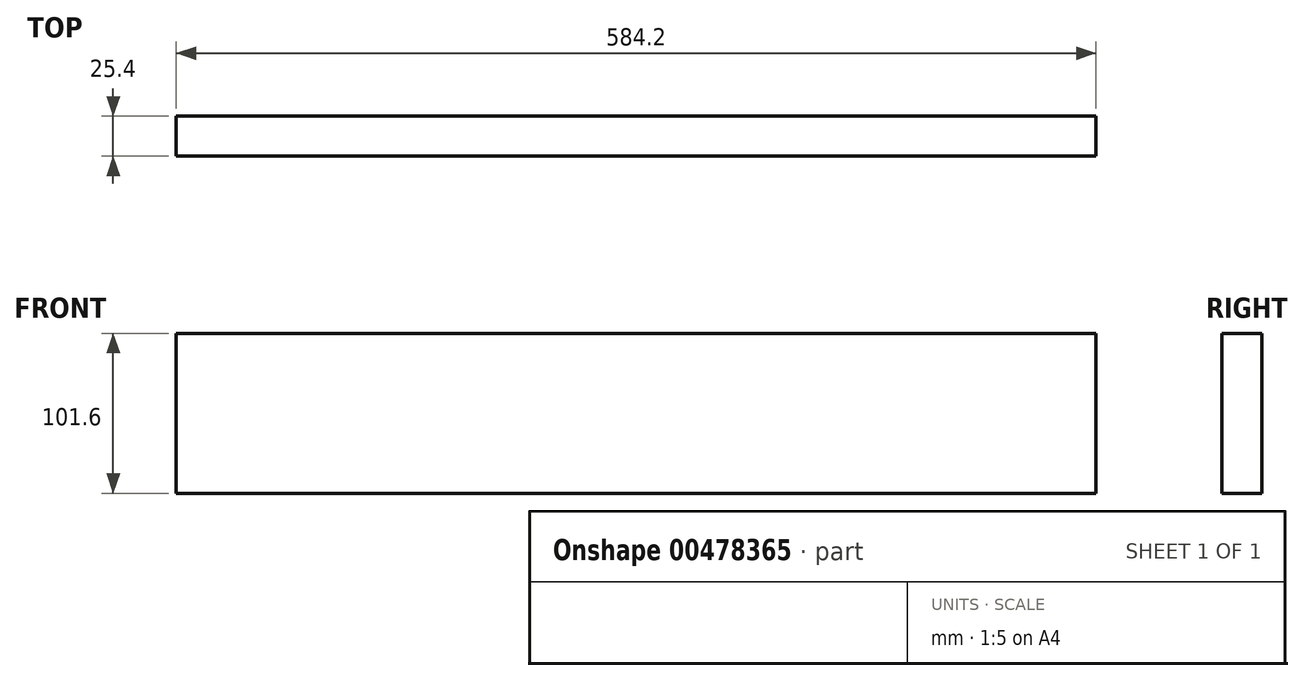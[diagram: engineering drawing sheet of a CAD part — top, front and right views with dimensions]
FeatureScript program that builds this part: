
annotation { "Feature Type Name" : "Feature", "Feature Type Description" : "" }
export const myFeature = defineFeature(function(context is Context, id is Id, definition is map)
    precondition{}
    {
        {
            var Q0;
            Q0=qCreatedBy(makeId("Front.planeOp"),FACE);
            var sketch = newSketch(context, id + "F0", { "sketchPlane" : qUnion([Q0])});
            skLineSegment(sketch, "E0.bottom", {"start": v(-229.27, -46.32) * mm, "end": v(354.93, -46.32) * mm});
            skLineSegment(sketch, "E0.top", {"start": v(-229.27, 55.28) * mm, "end": v(354.93, 55.28) * mm});
            skLineSegment(sketch, "E0.left", {"start": v(-229.27, -46.32) * mm, "end": v(-229.27, 55.28) * mm});
            skLineSegment(sketch, "E0.right", {"start": v(354.93, -46.32) * mm, "end": v(354.93, 55.28) * mm});
            skSolve(sketch);
        }
        {
            var Q0;
            Q0 = qSketchRegion(id + "F0", true);
            extrude(context, id + "F1", {"entities" : qUnion([Q0]), "depth" : 25.4 * mm, "offsetDistance" : 25.4 * mm});
        }
    });
